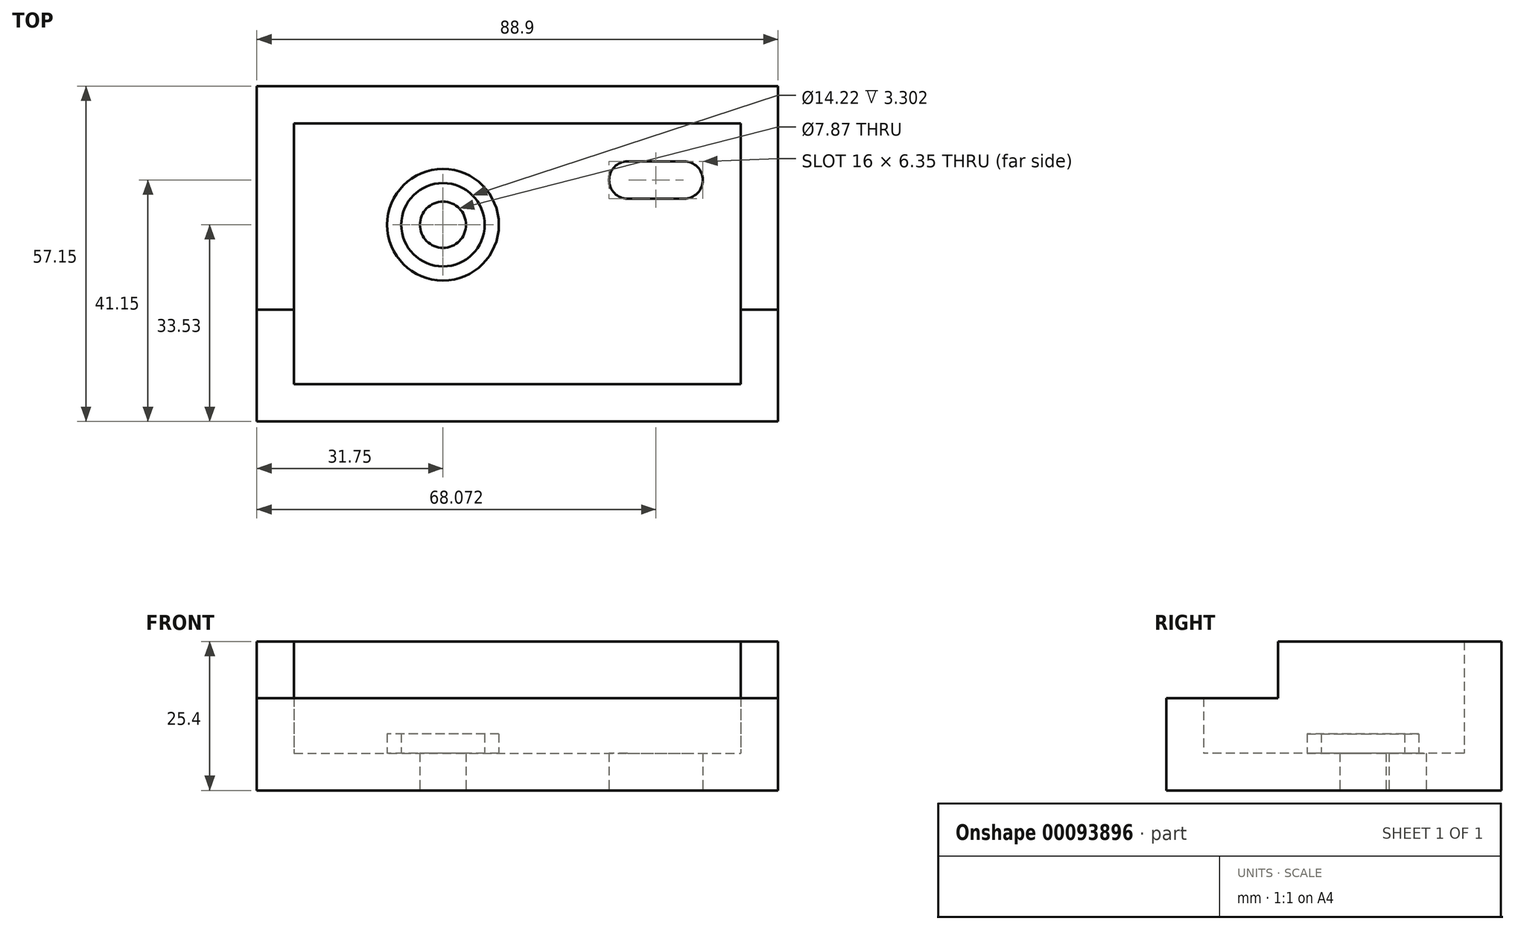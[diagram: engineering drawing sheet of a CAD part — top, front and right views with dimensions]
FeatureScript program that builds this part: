
annotation { "Feature Type Name" : "Feature", "Feature Type Description" : "" }
export const myFeature = defineFeature(function(context is Context, id is Id, definition is map)
    precondition{}
    {
        {
            var Q0;
            Q0=qCreatedBy(makeId("Top.planeOp"),FACE);
            var sketch = newSketch(context, id + "F0", { "sketchPlane" : qUnion([Q0])});
            skCircle(sketch, "E0", {"center": v(0, 0) * mm, "radius": 3.94 * mm});
            skCircle(sketch, "E1", {"center": v(0, 0) * mm, "radius": 7.11 * mm});
            skCircle(sketch, "E2", {"center": v(0, 0) * mm, "radius": 9.53 * mm});
            skLineSegment(sketch, "E3.bottom", {"start": v(-31.75, 23.62) * mm, "end": v(57.15, 23.62) * mm});
            skLineSegment(sketch, "E3.top", {"start": v(-31.75, -33.53) * mm, "end": v(57.15, -33.53) * mm});
            skLineSegment(sketch, "E3.left", {"start": v(-31.75, 23.62) * mm, "end": v(-31.75, -33.53) * mm});
            skLineSegment(sketch, "E3.right", {"start": v(57.15, 23.62) * mm, "end": v(57.15, -33.53) * mm});
            skLineSegment(sketch, "E4.0", {"start": v(-25.4, 17.27) * mm, "end": v(-25.4, -27.18) * mm});
            skLineSegment(sketch, "E4.1", {"start": v(-25.4, 17.27) * mm, "end": v(50.8, 17.27) * mm});
            skLineSegment(sketch, "E4.2", {"start": v(50.8, 17.27) * mm, "end": v(50.8, -27.18) * mm});
            skLineSegment(sketch, "E4.3", {"start": v(-25.4, -27.18) * mm, "end": v(50.8, -27.18) * mm});
            skLineSegment(sketch, "E5", {"start": v(41.15, 11.8) * mm, "end": v(41.15, 3.44) * mm, "construction": true});
            skLineSegment(sketch, "E6", {"start": v(31.5, 12.13) * mm, "end": v(31.5, 3.1) * mm, "construction": true});
            skLineSegment(sketch, "E7", {"start": v(31.5, 10.8) * mm, "end": v(41.15, 10.8) * mm});
            skLineSegment(sketch, "E8", {"start": v(31.5, 4.44) * mm, "end": v(41.15, 4.44) * mm});
            skArc(sketch, "E9", {"start": v(41.15, 4.44) * mm, "mid": v(44.32, 7.62) * mm, "end": v(41.15, 10.8) * mm});
            skArc(sketch, "E10", {"start": v(31.5, 10.8) * mm, "mid": v(28.32, 7.62) * mm, "end": v(31.5, 4.44) * mm});
            skLineSegment(sketch, "E11", {"start": v(-31.75, -14.48) * mm, "end": v(-25.4, -14.48) * mm});
            skLineSegment(sketch, "E12", {"start": v(50.8, -14.48) * mm, "end": v(57.15, -14.48) * mm});
            skSolve(sketch);
        }
        {
            var Q0;
            {var subQ4=sQuery(id+"F0.wireOp",EDGE,"E3.bottom");Q0=makeQuery(id+"F0.imprint","IMPRINT",FACE,{"disambiguationData":[TD([[makeQuery(id+"F0.imprint","IMPRINT",EDGE,{"derivedFrom":subQ4}),-1.0]])]});}
            extrude(context, id + "F1", {"entities" : qUnion([Q0]), "depth" : 25.4 * mm});
        }
        {
            var Q0;
            {var subQ4=sQuery(id+"F0.wireOp",EDGE,"E3.top");Q0=makeQuery(id+"F0.imprint","IMPRINT",FACE,{"disambiguationData":[TD([[makeQuery(id+"F0.imprint","IMPRINT",EDGE,{"derivedFrom":subQ4}),1.0]])]});}
            extrude(context, id + "F2", {"entities" : qUnion([Q0]), "operationType" : NewBodyOperationType.ADD, "depth" : 15.75 * mm});
        }
        {
            var Q0;
            Q0=makeQuery(id+"F0.imprint","IMPRINT",FACE,{"disambiguationData":[TD([[makeQuery(id+"F0.imprint","IMPRINT",EDGE,{"derivedFrom":sQuery(id+"F0.wireOp",EDGE,"E2")}),-1.0]])]});
            extrude(context, id + "F3", {"entities" : qUnion([Q0]), "operationType" : NewBodyOperationType.ADD, "depth" : 6.35 * mm});
        }
        {
            var Q0;
            Q0=makeQuery(id+"F0.imprint","IMPRINT",FACE,{"disambiguationData":[TD([[makeQuery(id+"F0.imprint","IMPRINT",EDGE,{"derivedFrom":sQuery(id+"F0.wireOp",EDGE,"E1")}),-1.0]])]});
            extrude(context, id + "F4", {"entities" : qUnion([Q0]), "operationType" : NewBodyOperationType.ADD, "depth" : 9.65 * mm});
        }
        {
            var Q0;
            Q0=makeQuery(id+"F0.imprint","IMPRINT",FACE,{"disambiguationData":[TD([[makeQuery(id+"F0.imprint","IMPRINT",EDGE,{"derivedFrom":sQuery(id+"F0.wireOp",EDGE,"E0")}),-1.0]])]});
            extrude(context, id + "F5", {"entities" : qUnion([Q0]), "operationType" : NewBodyOperationType.ADD, "depth" : 6.35 * mm});
        }
    });
